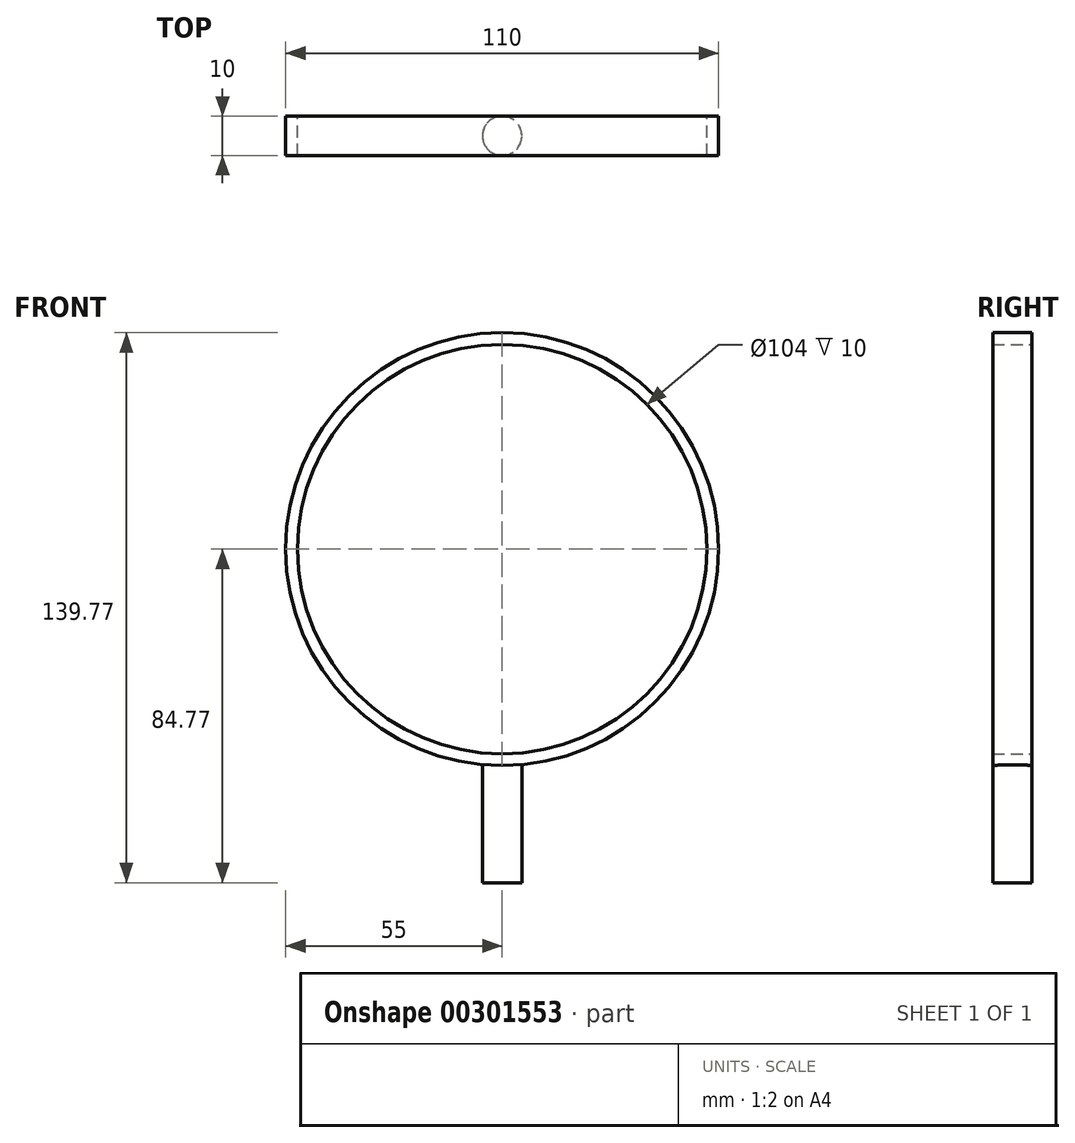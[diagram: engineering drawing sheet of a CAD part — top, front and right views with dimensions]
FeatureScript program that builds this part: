
annotation { "Feature Type Name" : "Feature", "Feature Type Description" : "" }
export const myFeature = defineFeature(function(context is Context, id is Id, definition is map)
    precondition{}
    {
        {
            var Q0;
            Q0=qCreatedBy(makeId("Front.planeOp"),FACE);
            var sketch = newSketch(context, id + "F0", { "sketchPlane" : qUnion([Q0])});
            skCircle(sketch, "E0", {"center": v(0, 0) * mm, "radius": 52 * mm});
            skArc(sketch, "E1", {"start": v(5, -54.77) * mm, "mid": v(0, 55) * mm, "end": v(-5, -54.77) * mm});
            skLineSegment(sketch, "E2.top", {"start": v(5, -84.77) * mm, "end": v(-5, -84.77) * mm});
            skLineSegment(sketch, "E2.left", {"start": v(5, -54.77) * mm, "end": v(5, -84.77) * mm});
            skLineSegment(sketch, "E2.right", {"start": v(-5, -54.77) * mm, "end": v(-5, -84.77) * mm});
            skSolve(sketch);
        }
        {
            var Q0;
            Q0 = qSketchRegion(id + "F0", true);
            extrude(context, id + "F1", {"entities" : qUnion([Q0]), "depth" : 10 * mm});
        }
        {
            var Q0;
            Q0=makeQuery(id+"F1.opExtrude","CAP_EDGE",EDGE,{"disambiguationData":[OSD([sQuery(id+"F0.wireOp",EDGE,"E2.left")])],"isStart":false});
            var Q1;
            Q1=makeQuery(id+"F1.opExtrude","CAP_EDGE",EDGE,{"disambiguationData":[OSD([sQuery(id+"F0.wireOp",EDGE,"E2.right")])],"isStart":false});
            var Q2;
            Q2=makeQuery(id+"F1.opExtrude","CAP_EDGE",EDGE,{"disambiguationData":[OSD([sQuery(id+"F0.wireOp",EDGE,"E2.right")])],"isStart":true});
            var Q3;
            Q3=makeQuery(id+"F1.opExtrude","CAP_EDGE",EDGE,{"disambiguationData":[OSD([sQuery(id+"F0.wireOp",EDGE,"E2.left")])],"isStart":true});
            fillet(context, id + "F2", {"entities" : qUnion([Q0, Q1, Q2, Q3]), "radius" : 5 * mm, "tangentPropagation" : true, "allowEdgeOverflow" : false});
        }
    });
